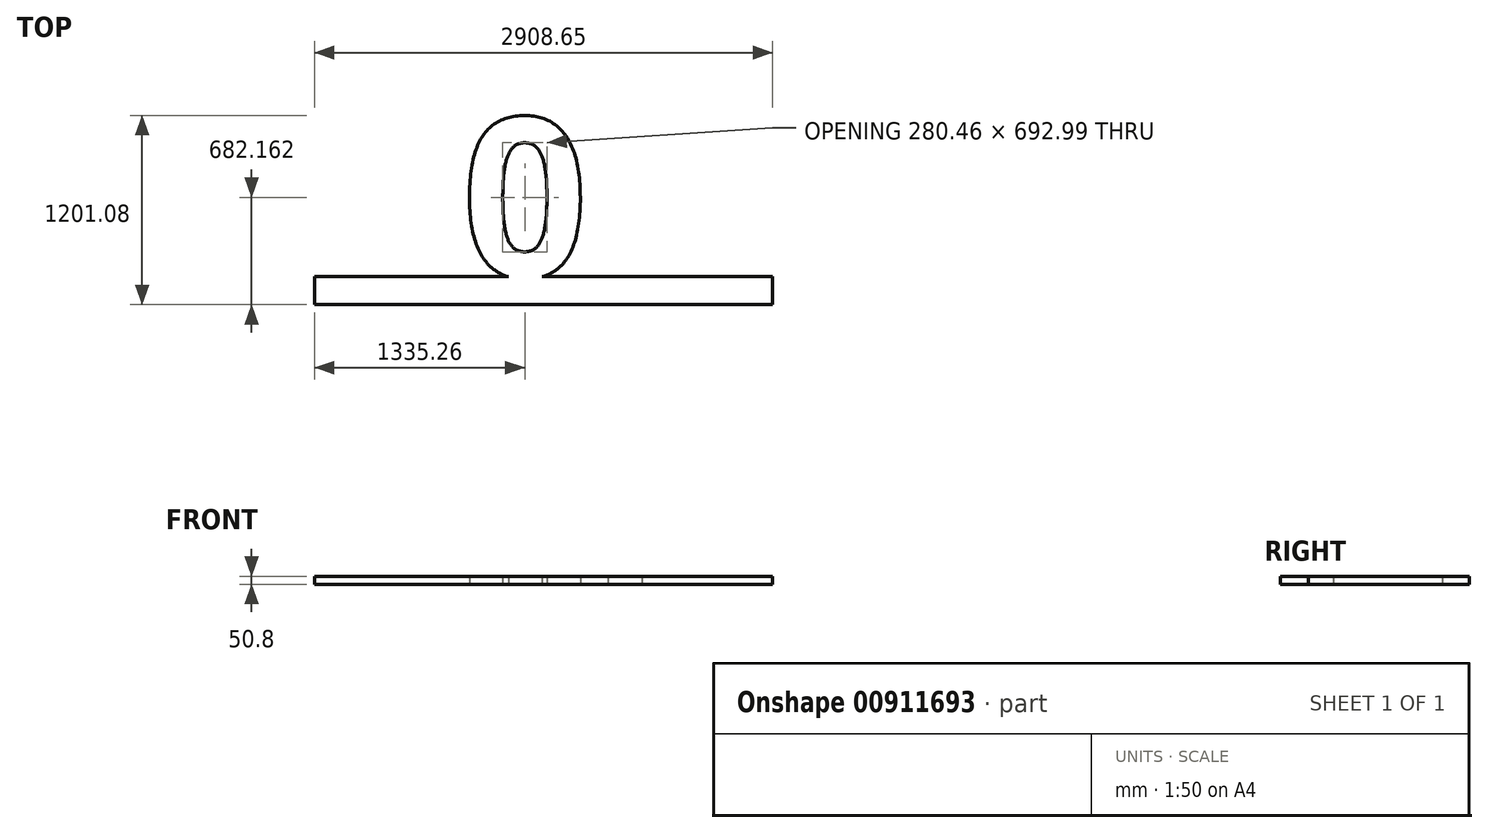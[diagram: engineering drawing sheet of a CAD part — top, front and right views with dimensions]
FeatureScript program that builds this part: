
annotation { "Feature Type Name" : "Feature", "Feature Type Description" : "" }
export const myFeature = defineFeature(function(context is Context, id is Id, definition is map)
    precondition{}
    {
        {
            var Q0;
            Q0=qCreatedBy(makeId("Top.planeOp"),FACE);
            var sketch = newSketch(context, id + "F0", { "sketchPlane" : qUnion([Q0])});
            skLineSegment(sketch, "E0.bottom", {"start": v(-177.37, -545.52) * mm, "end": v(2731.28, -545.52) * mm});
            skLineSegment(sketch, "E0.top", {"start": v(-177.37, -367.72) * mm, "end": v(2731.28, -367.72) * mm});
            skLineSegment(sketch, "E0.left", {"start": v(-177.37, -545.52) * mm, "end": v(-177.37, -367.72) * mm});
            skLineSegment(sketch, "E0.right", {"start": v(2731.28, -545.52) * mm, "end": v(2731.28, -367.72) * mm});
            skText(sketch, "E1", { "text": "10H", "fontName": "OpenSans-Bold.ttf"});
            const initialGuessF0  = {"E1": [-0.05037, -0.36772, 1, 0, 1.016]};
            skSetInitialGuess(sketch, initialGuessF0);
            skSolve(sketch);
        }
        {
            var Q0;
            {var subQ0=sQuery(id+"F0.wireOp",EDGE,"E1.sketch_text.stroke-12");var subQ1=sQuery(id+"F0.wireOp",EDGE,"E0.top");var subQ2=makeQuery(id+"F0.imprint","INTERSECT",VERTEX,{"derivedFrom":[subQ1,subQ0]});Q0=makeQuery(id+"F0.imprint","IMPRINT",FACE,{"disambiguationData":[TD([[makeQuery(id+"F0.imprint","IMPRINT",EDGE,{"disambiguationData":[TD([[subQ2,-1.0]])],"derivedFrom":subQ1}),-1.0]])]});}
            var Q1;
            {var subQ6=sQuery(id+"F0.wireOp",EDGE,"E1.sketch_text.stroke-10");Q1=makeQuery(id+"F0.imprint","IMPRINT",FACE,{"disambiguationData":[TD([[makeQuery(id+"F0.imprint","IMPRINT",EDGE,{"derivedFrom":subQ6}),-1.0]])]});}
            var Q2;
            Q2=makeQuery(id+"F0.imprint","IMPRINT",FACE,{"disambiguationData":[TD([[makeQuery(id+"F0.imprint","IMPRINT",EDGE,{"derivedFrom":sQuery(id+"F0.wireOp",EDGE,"E0.bottom")}),1.0]])]});
            var Q3;
            Q3=makeQuery(id+"F0.imprint","IMPRINT",FACE,{"disambiguationData":[TD([[makeQuery(id+"F0.imprint","IMPRINT",EDGE,{"derivedFrom":sQuery(id+"F0.wireOp",EDGE,"E1.sketch_text.stroke-26")}),-1.0]])]});
            var Q4;
            Q4=makeQuery(id+"F0.imprint","IMPRINT",FACE,{"disambiguationData":[TD([[makeQuery(id+"F0.imprint","IMPRINT",EDGE,{"derivedFrom":sQuery(id+"F0.wireOp",EDGE,"E1.sketch_text.stroke-0")}),-1.0]])]});
            extrude(context, id + "F1", {"entities" : qUnion([Q0, Q1, Q2, Q3, Q4]), "depth" : 50.8 * mm, "offsetDistance" : 25.4 * mm});
        }
    });
